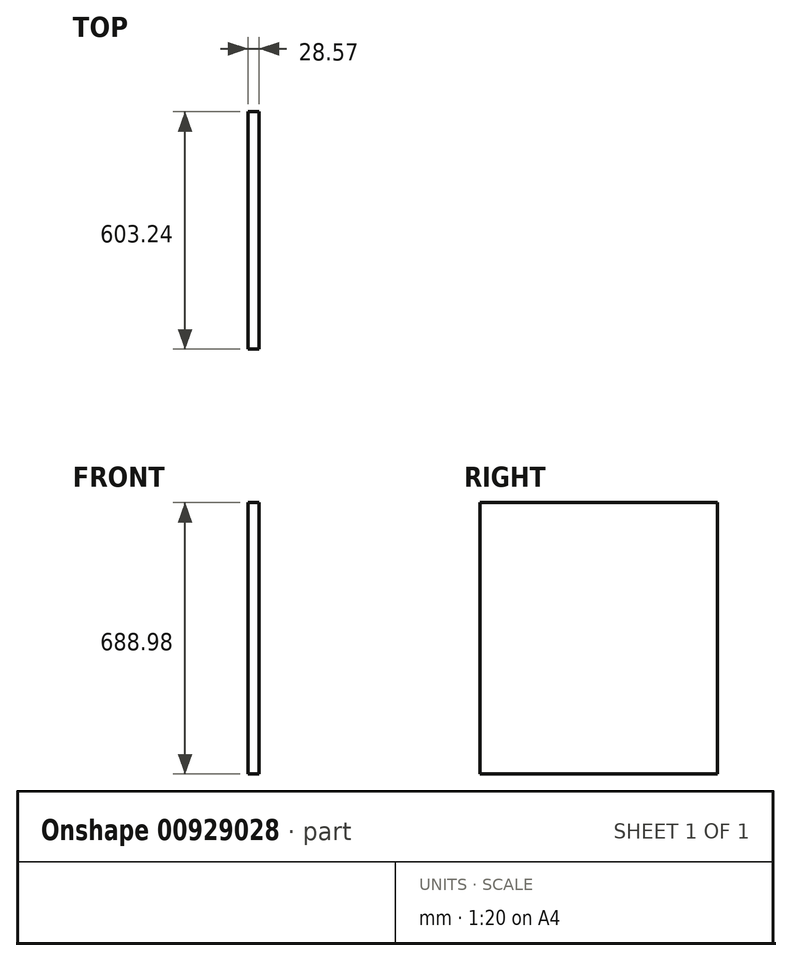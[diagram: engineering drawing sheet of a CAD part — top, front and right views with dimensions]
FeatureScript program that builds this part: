
annotation { "Feature Type Name" : "Feature", "Feature Type Description" : "" }
export const myFeature = defineFeature(function(context is Context, id is Id, definition is map)
    precondition{}
    {
        {
            var Q0;
            Q0=qCreatedBy(makeId("Right.planeOp"),FACE);
            var sketch = newSketch(context, id + "F0", { "sketchPlane" : qUnion([Q0])});
            skLineSegment(sketch, "E0.bottom", {"start": v(301.63, 344.49) * mm, "end": v(-301.63, 344.49) * mm});
            skLineSegment(sketch, "E0.top", {"start": v(301.62, -344.49) * mm, "end": v(-301.63, -344.49) * mm});
            skLineSegment(sketch, "E0.left", {"start": v(301.62, 344.49) * mm, "end": v(301.62, -344.49) * mm});
            skLineSegment(sketch, "E0.right", {"start": v(-301.63, 344.49) * mm, "end": v(-301.63, -344.49) * mm});
            skPoint(sketch, "E0.middle", {"position": v(0, 0) * mm});
            skSolve(sketch);
        }
        {
            var Q0;
            Q0=makeQuery(id+"F0.imprint","IMPRINT",FACE,{"disambiguationData":[TD([[makeQuery(id+"F0.imprint","IMPRINT",EDGE,{"derivedFrom":sQuery(id+"F0.wireOp",EDGE,"E0.bottom")}),1.0]])]});
            extrude(context, id + "F1", {"entities" : qUnion([Q0]), "depth" : 28.57 * mm, "offsetDistance" : 25.4 * mm});
        }
    });
